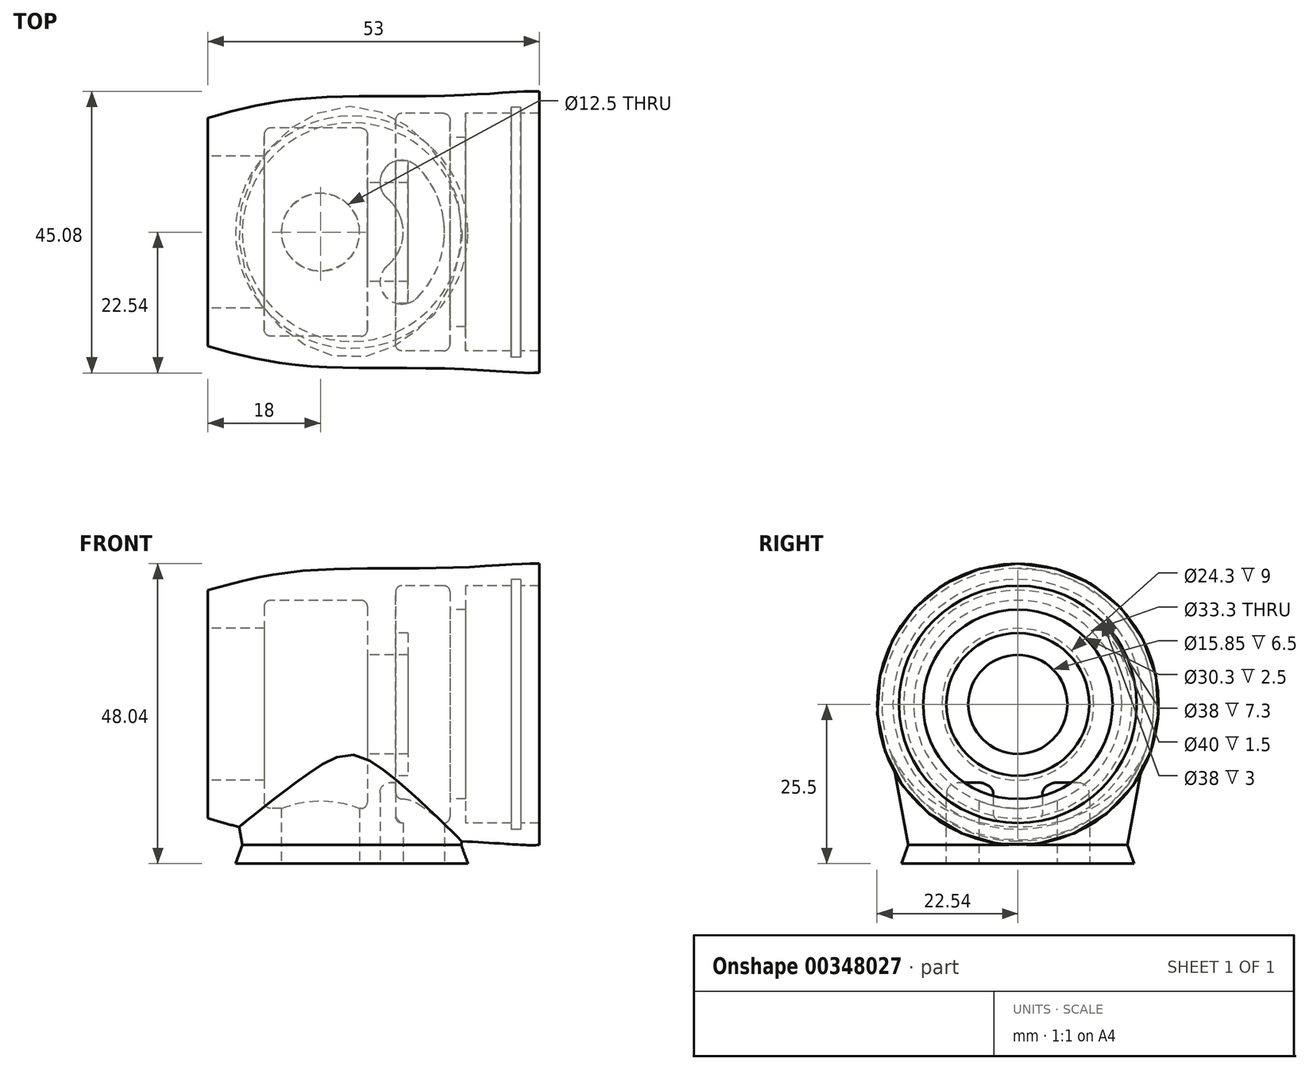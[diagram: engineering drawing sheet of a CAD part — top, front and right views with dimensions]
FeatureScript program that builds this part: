
annotation { "Feature Type Name" : "Feature", "Feature Type Description" : "" }
export const myFeature = defineFeature(function(context is Context, id is Id, definition is map)
    precondition{}
    {
        {
            var Q0;
            Q0=qCreatedBy(makeId("Front.planeOp"),FACE);
            var sketch = newSketch(context, id + "F0", { "sketchPlane" : qUnion([Q0])});
            skLineSegment(sketch, "E0", {"start": v(-26.5, 0) * mm, "end": v(26.5, 0) * mm, "construction": true});
            skPoint(sketch, "E1", {"position": v(26.5, 22.5) * mm});
            skPoint(sketch, "E2", {"position": v(-26.5, 18.25) * mm});
            skFitSpline(sketch, "E3", {"points": [v(-26.5, 18.25) * mm, v(-8.41, 21.57) * mm, v(12.15, 21.85) * mm, v(24.65, 22.53) * mm, v(26.5, 22.5) * mm], "startDerivative": vector(67.62, 20.36) * mm, "endDerivative": vector(16.75, -0.87) * mm});
            skLineSegment(sketch, "E4", {"start": v(-26.5, 12.15) * mm, "end": v(-17.5, 12.15) * mm});
            skLineSegment(sketch, "E5", {"start": v(-26.5, 18.25) * mm, "end": v(-26.5, 12.15) * mm});
            skLineSegment(sketch, "E6", {"start": v(-1, 7.92) * mm, "end": v(5.5, 7.92) * mm});
            skLineSegment(sketch, "E7", {"start": v(-17.5, 12.15) * mm, "end": v(-17.5, 15.65) * mm});
            skLineSegment(sketch, "E8", {"start": v(-16.5, 16.65) * mm, "end": v(-2, 16.65) * mm});
            skLineSegment(sketch, "E9", {"start": v(-1, 15.65) * mm, "end": v(-1, 7.92) * mm});
            skPoint(sketch, "E10.visualSharp", {"position": v(-17.5, 16.65) * mm});
            skArc(sketch, "E10.filletArc", {"start": v(-16.5, 16.65) * mm, "mid": v(-17.2, 16.36) * mm, "end": v(-17.5, 15.65) * mm});
            skPoint(sketch, "E11.visualSharp", {"position": v(-1, 16.65) * mm});
            skArc(sketch, "E11.filletArc", {"start": v(-1, 15.65) * mm, "mid": v(-1.3, 16.36) * mm, "end": v(-2, 16.65) * mm});
            skLineSegment(sketch, "E12", {"start": v(26.5, 19) * mm, "end": v(23.5, 19) * mm});
            skLineSegment(sketch, "E13", {"start": v(26.5, 22.5) * mm, "end": v(26.5, 19) * mm});
            skLineSegment(sketch, "E14", {"start": v(14.7, 19) * mm, "end": v(14.7, 15.15) * mm});
            skLineSegment(sketch, "E15", {"start": v(14.7, 15.15) * mm, "end": v(12.2, 15.15) * mm});
            skLineSegment(sketch, "E16", {"start": v(12.2, 15.15) * mm, "end": v(12.2, 18) * mm});
            skLineSegment(sketch, "E17", {"start": v(11.2, 19) * mm, "end": v(4.5, 19) * mm});
            skLineSegment(sketch, "E18", {"start": v(5.5, 11.42) * mm, "end": v(5.5, 7.92) * mm});
            skPoint(sketch, "E19.visualSharp", {"position": v(12.2, 19) * mm});
            skArc(sketch, "E19.filletArc", {"start": v(12.2, 18) * mm, "mid": v(11.9, 18.7) * mm, "end": v(11.2, 19) * mm});
            skPoint(sketch, "E20", {"position": v(23.5, 19) * mm});
            skPoint(sketch, "E21", {"position": v(22, 19) * mm});
            skLineSegment(sketch, "E22", {"start": v(22, 20) * mm, "end": v(23.5, 20) * mm});
            skLineSegment(sketch, "E23", {"start": v(23.5, 20) * mm, "end": v(23.5, 19) * mm});
            skLineSegment(sketch, "E24", {"start": v(22, 20) * mm, "end": v(22, 19) * mm});
            skLineSegment(sketch, "E25.trimOffspring", {"start": v(22, 19) * mm, "end": v(14.7, 19) * mm});
            skLineSegment(sketch, "E26", {"start": v(5.5, 11.42) * mm, "end": v(3.5, 11.42) * mm});
            skLineSegment(sketch, "E27", {"start": v(3.5, 11.42) * mm, "end": v(3.5, 18) * mm});
            skPoint(sketch, "E28.visualSharp", {"position": v(3.5, 19) * mm});
            skArc(sketch, "E28.filletArc", {"start": v(4.5, 19) * mm, "mid": v(3.8, 18.7) * mm, "end": v(3.5, 18) * mm});
            skSolve(sketch);
        }
        {
            var Q0;
            Q0=makeQuery(id+"F0.imprint","IMPRINT",FACE,{"disambiguationData":[TD([[makeQuery(id+"F0.imprint","IMPRINT",EDGE,{"derivedFrom":sQuery(id+"F0.wireOp",EDGE,"E3")}),-1.0]])]});
            var Q1;
            Q1=sQuery(id+"F0.wireOp",EDGE,"E0");
            revolve(context, id + "F1", {"entities" : qUnion([Q0]), "axis" : qUnion([Q1]), "revolveType" : RevolveType.FULL});
        }
        {
            var Q0;
            Q0=qCreatedBy(makeId("Top.planeOp"),FACE);
            cPlane(context, id + "F2", {"entities" : qUnion([Q0]), "cplaneType" : CPlaneType.OFFSET, "offset" : 22.5 * mm, "oppositeDirection" : true, "width" : 150 * mm, "height" : 150 * mm});
        }
        {
            var Q0;
            Q0=qCreatedBy(id+"F2.planeOp",FACE);
            var sketch = newSketch(context, id + "F3", { "sketchPlane" : qUnion([Q0])});
            skCircle(sketch, "E29", {"center": v(-3.5, 0) * mm, "radius": 17.5 * mm});
            skSolve(sketch);
        }
        {
            var Q0;
            Q0=makeQuery(id+"F3.imprint","IMPRINT",FACE,{"disambiguationData":[TD([[makeQuery(id+"F3.imprint","IMPRINT",EDGE,{"derivedFrom":sQuery(id+"F3.wireOp",EDGE,"E29")}),1.0]])]});
            extrude(context, id + "F4", {"entities" : qUnion([Q0]), "operationType" : NewBodyOperationType.ADD, "endBound" : BoundingType.UP_TO_NEXT, "depth" : 25 * mm, "hasDraft" : true, "draftAngle" : 10.5 * degree, "hasSecondDirection" : true, "secondDirectionOppositeDirection" : true, "secondDirectionDepth" : 3 * mm, "hasSecondDirectionDraft" : true, "secondDirectionDraftAngle" : 20 * degree});
        }
        {
            var Q0;
            Q0=makeQuery(id+"F4.opExtrude","CAP_FACE",FACE,{"disambiguationData":[OSD([sQuery(id+"F3.wireOp",EDGE,"E29")])],"isStart":true});
            var sketch = newSketch(context, id + "F5", { "sketchPlane" : qUnion([Q0])});
            skCircle(sketch, "E30", {"center": v(-8.5, 0) * mm, "radius": 6.25 * mm});
            skArc(sketch, "E31", {"start": v(6.97, 10.47) * mm, "mid": v(1.92, 10.37) * mm, "end": v(2.24, 5.32) * mm});
            skArc(sketch, "E32", {"start": v(2.24, -5.32) * mm, "mid": v(1.92, -10.37) * mm, "end": v(6.97, -10.47) * mm});
            skArc(sketch, "E33", {"start": v(2.24, -5.32) * mm, "mid": v(4.72, 0) * mm, "end": v(2.24, 5.32) * mm});
            skArc(sketch, "E34", {"start": v(6.97, -10.47) * mm, "mid": v(11.31, 0) * mm, "end": v(6.97, 10.47) * mm});
            skSolve(sketch);
        }
        {
            var Q0;
            Q0=makeQuery(id+"F5.imprint","IMPRINT",FACE,{"disambiguationData":[TD([[makeQuery(id+"F5.imprint","IMPRINT",EDGE,{"derivedFrom":sQuery(id+"F5.wireOp",EDGE,"E30")}),1.0]])]});
            var Q1;
            Q1=makeQuery(id+"F5.imprint","IMPRINT",FACE,{"disambiguationData":[TD([[makeQuery(id+"F5.imprint","IMPRINT",EDGE,{"derivedFrom":sQuery(id+"F5.wireOp",EDGE,"E31")}),1.0]])]});
            extrude(context, id + "F6", {"entities" : qUnion([Q0, Q1]), "operationType" : NewBodyOperationType.REMOVE, "oppositeDirection" : true, "depth" : 13 * mm});
        }
        {
            var Q0;
            Q0=makeQuery(id+"F6.boolean.opBoolean","COPY",EDGE,{"derivedFrom":makeQuery(id+"F6.opExtrude","CAP_EDGE",EDGE,{"disambiguationData":[OSD([sQuery(id+"F5.wireOp",EDGE,"E31")])],"isStart":false})});
            var Q1;
            Q1=makeQuery(id+"F6.boolean.opBoolean","COPY",EDGE,{"derivedFrom":makeQuery(id+"F6.opExtrude","CAP_EDGE",EDGE,{"disambiguationData":[OSD([sQuery(id+"F5.wireOp",EDGE,"E32")])],"isStart":false})});
            fillet(context, id + "F7", {"entities" : qUnion([Q0, Q1]), "radius" : 1.69 * mm, "tangentPropagation" : true, "allowEdgeOverflow" : false});
        }
    });
